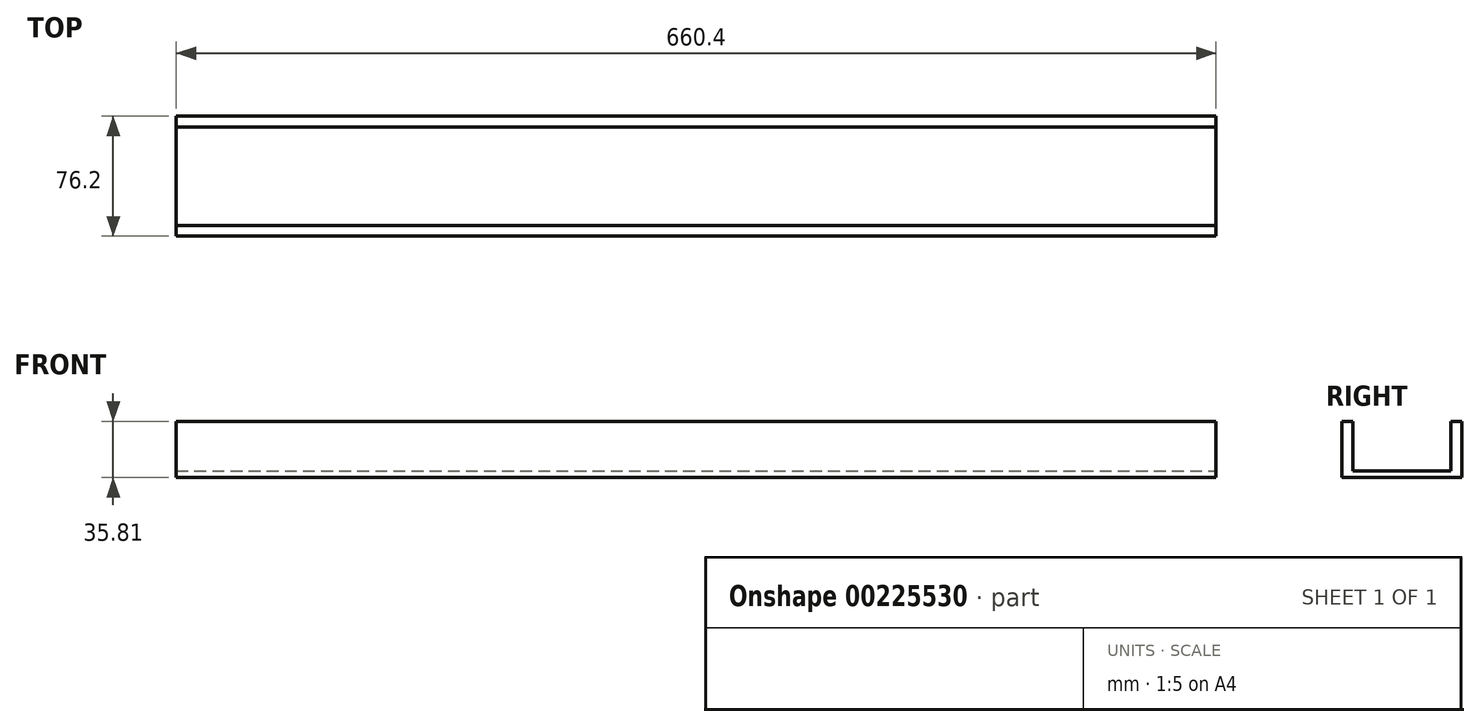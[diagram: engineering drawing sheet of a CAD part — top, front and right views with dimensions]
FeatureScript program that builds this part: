
annotation { "Feature Type Name" : "Feature", "Feature Type Description" : "" }
export const myFeature = defineFeature(function(context is Context, id is Id, definition is map)
    precondition{}
    {
        {
            var Q0;
            Q0=qCreatedBy(makeId("Top.planeOp"),FACE);
            var sketch = newSketch(context, id + "F0", { "sketchPlane" : qUnion([Q0])});
            skLineSegment(sketch, "E0.bottom", {"start": v(-136.18, -40.28) * mm, "end": v(524.22, -40.28) * mm});
            skLineSegment(sketch, "E0.top", {"start": v(-136.18, 35.92) * mm, "end": v(524.22, 35.92) * mm});
            skLineSegment(sketch, "E0.left", {"start": v(-136.18, -40.28) * mm, "end": v(-136.18, 35.92) * mm});
            skLineSegment(sketch, "E0.right", {"start": v(524.22, -40.28) * mm, "end": v(524.22, 35.92) * mm});
            skSolve(sketch);
        }
        {
            var Q0;
            Q0 = qSketchRegion(id + "F0", true);
            extrude(context, id + "F1", {"entities" : qUnion([Q0]), "depth" : 35.81 * mm});
        }
        {
            var Q0;
            Q0=makeQuery(id+"F1.opExtrude","SWEPT_FACE",FACE,{"disambiguationData":[OSD([sQuery(id+"F0.wireOp",EDGE,"E0.right")])]});
            var sketch = newSketch(context, id + "F2", { "sketchPlane" : qUnion([Q0])});
            skLineSegment(sketch, "E1.bottom", {"start": v(28.99, 35.81) * mm, "end": v(-33.35, 35.81) * mm});
            skLineSegment(sketch, "E1.top", {"start": v(28.99, 4.32) * mm, "end": v(-33.35, 4.32) * mm});
            skLineSegment(sketch, "E1.left", {"start": v(28.99, 35.81) * mm, "end": v(28.99, 4.32) * mm});
            skLineSegment(sketch, "E1.right", {"start": v(-33.35, 35.81) * mm, "end": v(-33.35, 4.32) * mm});
            skSolve(sketch);
        }
        {
            var Q0;
            Q0 = qSketchRegion(id + "F2", true);
            extrude(context, id + "F3", {"entities" : qUnion([Q0]), "operationType" : NewBodyOperationType.REMOVE, "endBound" : BoundingType.THROUGH_ALL, "oppositeDirection" : true, "depth" : 25.4 * mm});
        }
    });
